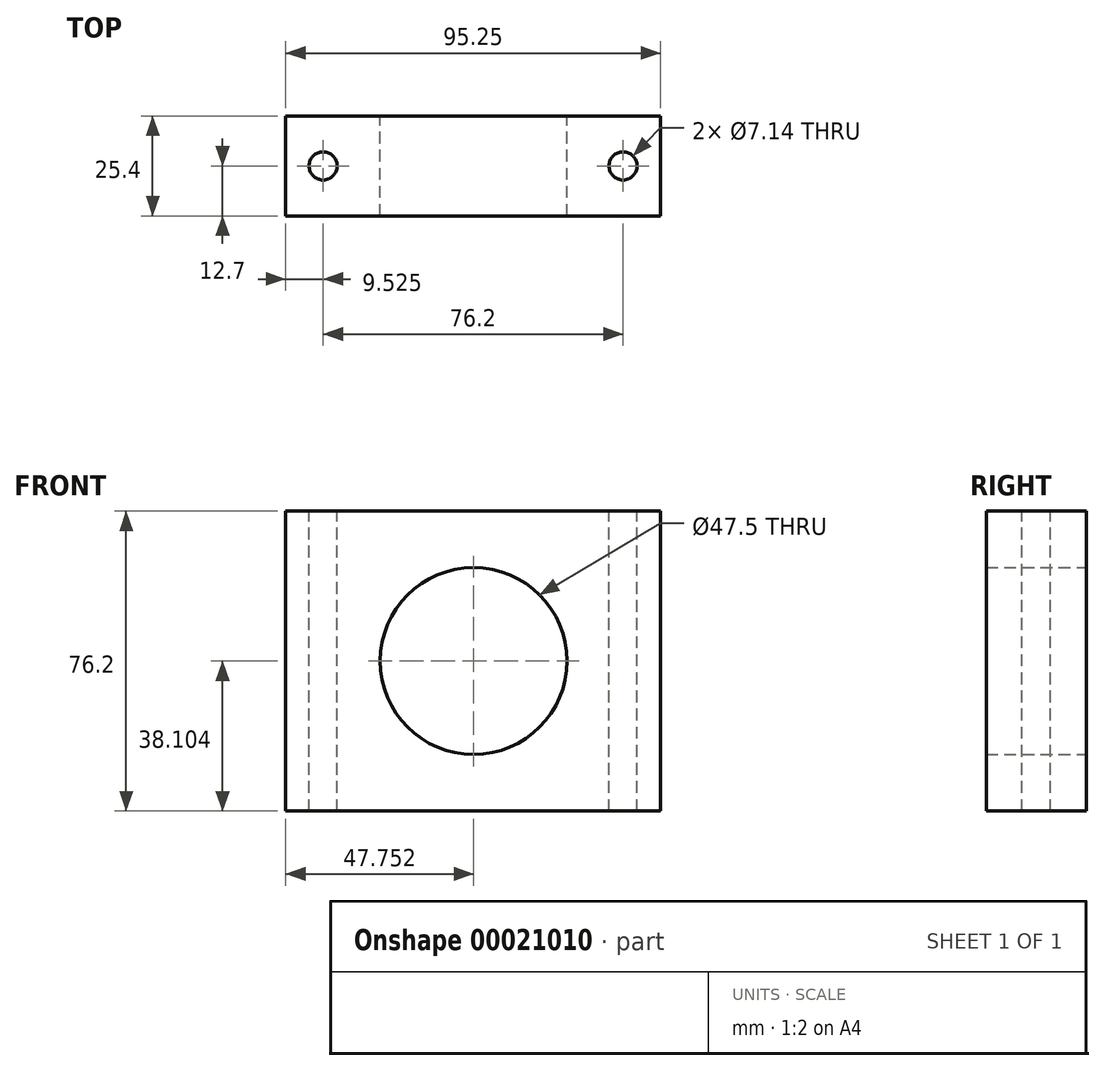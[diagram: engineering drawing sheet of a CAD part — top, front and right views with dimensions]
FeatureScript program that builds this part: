
annotation { "Feature Type Name" : "Feature", "Feature Type Description" : "" }
export const myFeature = defineFeature(function(context is Context, id is Id, definition is map)
    precondition{}
    {
        {
            var Q0;
            Q0=qCreatedBy(makeId("Front.planeOp"),FACE);
            var sketch = newSketch(context, id + "F0", { "sketchPlane" : qUnion([Q0])});
            skLineSegment(sketch, "E0.bottom", {"start": v(-63.52, 39.04) * mm, "end": v(31.73, 39.04) * mm});
            skLineSegment(sketch, "E0.top", {"start": v(-63.52, -37.16) * mm, "end": v(31.73, -37.16) * mm});
            skLineSegment(sketch, "E0.left", {"start": v(-63.52, 39.04) * mm, "end": v(-63.52, -37.16) * mm});
            skLineSegment(sketch, "E0.right", {"start": v(31.73, 39.04) * mm, "end": v(31.73, -37.16) * mm});
            skLineSegment(sketch, "E1.0", {"start": v(-15.77, 39.04) * mm, "end": v(-15.77, -37.16) * mm});
            skCircle(sketch, "E2", {"center": v(-15.77, 0.94) * mm, "radius": 23.75 * mm});
            skSolve(sketch);
        }
        {
            var Q0;
            Q0=makeQuery(id+"F0.imprint","IMPRINT",FACE,{"disambiguationData":[TD([[makeQuery(id+"F0.imprint","IMPRINT",EDGE,{"derivedFrom":sQuery(id+"F0.wireOp",EDGE,"E0.bottom")}),-1.0]])]});
            extrude(context, id + "F1", {"entities" : qUnion([Q0]), "depth" : 25.4 * mm});
        }
        {
            var Q0;
            Q0=makeQuery(id+"F1.opExtrude","SWEPT_FACE",FACE,{"disambiguationData":[OSD([sQuery(id+"F0.wireOp",EDGE,"E0.bottom")])]});
            var sketch = newSketch(context, id + "F2", { "sketchPlane" : qUnion([Q0])});
            skLineSegment(sketch, "E3.0", {"start": v(-54, -25.4) * mm, "end": v(-54, 0) * mm});
            skLineSegment(sketch, "E4.0", {"start": v(22.2, -25.4) * mm, "end": v(22.2, 0) * mm});
            skLineSegment(sketch, "E5.0", {"start": v(-63.52, -12.7) * mm, "end": v(31.73, -12.7) * mm});
            skCircle(sketch, "E6", {"center": v(-54, -12.7) * mm, "radius": 3.57 * mm});
            skCircle(sketch, "E7", {"center": v(22.2, -12.7) * mm, "radius": 3.57 * mm});
            skSolve(sketch);
        }
        {
            var Q0;
            Q0 = qSketchRegion(id + "F2", true);
            extrude(context, id + "F3", {"entities" : qUnion([Q0]), "operationType" : NewBodyOperationType.REMOVE, "oppositeDirection" : true, "depth" : 127 * mm});
        }
    });
